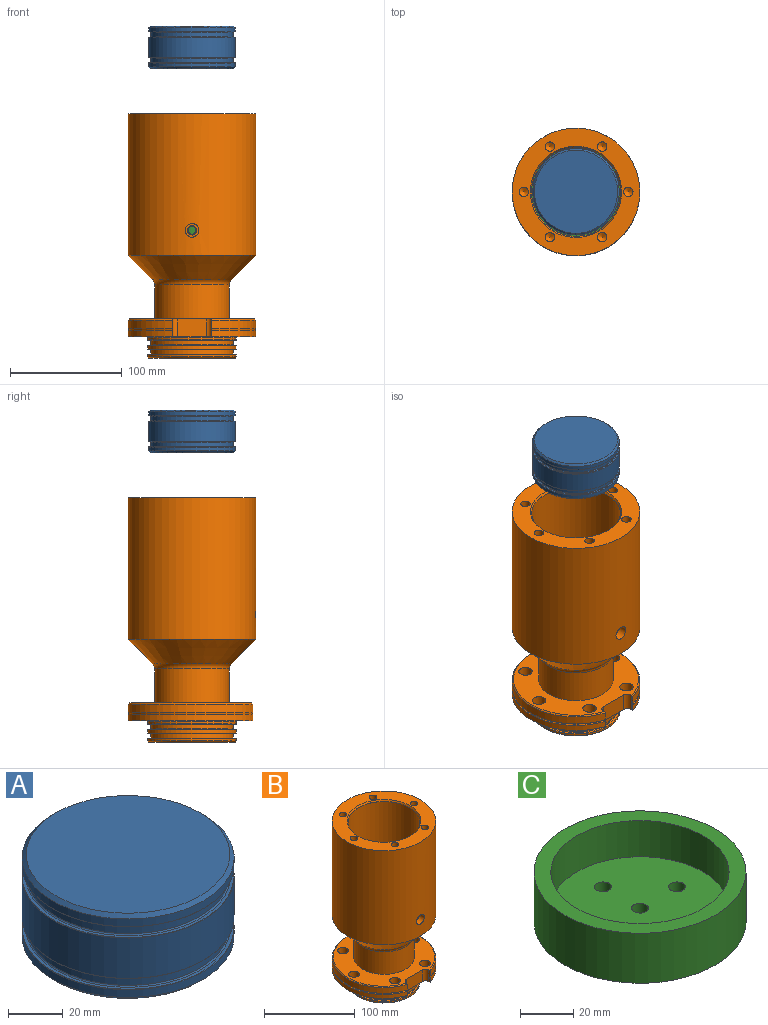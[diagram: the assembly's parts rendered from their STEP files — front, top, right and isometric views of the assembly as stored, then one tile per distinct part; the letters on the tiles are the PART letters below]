
ASSEMBLY  parts=3 mates=2
PART A: 21 faces, bbox 83.9x83.9x38.1 mm
  f0: cylinder r=36.86mm len=73.71mm, axis (0,0,1), area 882.3mm2, adj f1,f20
  f1: torus R=37.36mm, axis (0,0,1), area 185.7mm2, adj f0,f2
  f2: plane 77.22x77.22mm, normal (0,0,1), area 297.1mm2, adj f1,f3
  f3: torus R=38.61mm, axis (0,0,1), area 48.5mm2, adj f2,f4
  f4: cylinder r=38.73mm len=77.47mm, axis (0,0,1), area 4389.1mm2, adj f3,f5
  f5: torus R=38.61mm, axis (0,0,1), area 48.5mm2, adj f4,f6
  f6: plane 77.22x77.22mm, normal (0,0,-1), area 297.1mm2, adj f5,f7
  f7: torus R=37.36mm, axis (0,0,1), area 185.7mm2, adj f6,f8
  f8: cylinder r=36.86mm len=73.71mm, axis (0,0,1), area 882.3mm2, adj f7,f9
  f9: torus R=37.36mm, axis (0,0,1), area 185.7mm2, adj f8,f10
  f10: plane 77.22x77.22mm, normal (0,0,1), area 297.1mm2, adj f9,f11
  f11: torus R=38.61mm, axis (0,0,1), area 48.5mm2, adj f10,f12
  f12: cylinder r=38.73mm len=77.47mm, axis (0,0,1), area 834.5mm2, adj f11,f13
  f13: cone r=38.73mm half-angle=45deg, axis (0,0,1), area 514.2mm2, adj f12,f14
  f14: plane 74.42x74.42mm, normal (0,0,-1), area 4350mm2, adj f13
  f15: plane 74.42x74.42mm, normal (0,0,1), area 4350mm2, adj f16
  f16: cone r=38.73mm half-angle=45deg, axis (0,0,-1), area 514.2mm2, adj f15,f17
  f17: cylinder r=38.73mm len=77.47mm, axis (0,0,1), area 834.5mm2, adj f16,f18
  f18: torus R=38.61mm, axis (0,0,1), area 48.5mm2, adj f17,f19
  f19: plane 77.22x77.22mm, normal (0,0,-1), area 297.1mm2, adj f18,f20
  f20: torus R=37.36mm, axis (0,0,1), area 185.7mm2, adj f0,f19
PART B: 69 faces, bbox 124.9x121.9x218.8 mm
  f0: cylinder r=3.45mm len=7.11mm, axis (0,-1,0), area 153.4mm2, adj f1,f63,f66,f67
  f1: cylinder r=39.74mm len=129.98mm, axis (0,0,-1), area 32416.5mm2, adj f0,f18,f19,f63,f66
  f2: cylinder r=57.15mm len=127mm, axis (0,0,-1), area 45484.2mm2, adj f21,f22,f65
  f3: cylinder r=57.15mm len=114.3mm, axis (0,0,-1), area 2527mm2, adj f6,f7,f58,f59
  f4: cylinder r=57.15mm len=114.3mm, axis (0,0,-1), area 1807.5mm2, adj f7,f8,f58,f59
  f5: plane 112.14x109.34mm, normal (0,0,1), area 5443mm2, adj f6,f24,f52,f53,f54,f55,f56,f57
  f6: cone r=57.15mm half-angle=45deg, axis (0,0,-1), area 487.8mm2, adj f3,f5,f58,f59
  f7: torus R=57.15mm, axis (0,0,-1), area 766.9mm2, adj f3,f4,f58,f59
  f8: plane 114.3x111.55mm, normal (0,0,-1), area 4347.6mm2, adj f4,f25,f52,f53,f54,f55,f56,f57
  f9: plane 79.1x79.1mm, normal (0,0,1), area 521.8mm2, adj f10,f39
  f10: torus R=39.55mm, axis (0,0,-1), area 49.7mm2, adj f9,f11
  f11: cylinder r=39.67mm len=79.35mm, axis (0,0,-1), area 459.5mm2, adj f10,f12
  f12: cone r=39.67mm half-angle=45deg, axis (0,0,1), area 374.7mm2, adj f11,f13
  f13: plane 77.19x77.19mm, normal (0,0,-1), area 1545.2mm2, adj f12,f14
  f14: cone r=31.59mm half-angle=30deg, axis (0,0,-1), area 2572.9mm2, adj f13,f15
  f15: cylinder r=24.26mm len=72.39mm, axis (0,0,-1), area 11033mm2, adj f14,f16
  f16: plane 48.51x48.51mm, normal (0,0,-1), area 57.6mm2, adj f15,f17
  f17: cylinder r=23.88mm len=47.75mm, axis (0,0,-1), area 266.7mm2, adj f16,f18
  f18: plane 79.48x79.48mm, normal (0,0,1), area 3170.1mm2, adj f1,f17
  f19: torus R=39.99mm, axis (0,0,-1), area 33.2mm2, adj f1,f20
  f20: cone r=39.77mm half-angle=30deg, axis (0,0,1), area 539.8mm2, adj f19,f21
  f21: plane 114.3x114.3mm, normal (0,0,1), area 4686.3mm2, adj f2,f20,f41,f43,f45,f47,f49,f51
  f22: cone r=57.15mm half-angle=45deg, axis (0,0,1), area 8987mm2, adj f2,f23
  f23: torus R=39.75mm, axis (0,0,-1), area 1066.5mm2, adj f22,f24
  f24: cylinder r=33.4mm len=66.8mm, axis (0,0,-1), area 6377.7mm2, adj f5,f23
  f25: torus R=39.67mm, axis (0,0,-1), area 394.6mm2, adj f8,f26
  f26: cylinder r=39.67mm len=79.35mm, axis (0,0,-1), area 474.9mm2, adj f25,f27
  f27: torus R=39.55mm, axis (0,0,-1), area 49.7mm2, adj f26,f28
  f28: plane 79.1x79.1mm, normal (0,0,-1), area 521.8mm2, adj f27,f29
  f29: torus R=37.39mm, axis (0,0,-1), area 185.8mm2, adj f28,f30
  f30: cylinder r=36.88mm len=73.76mm, axis (0,0,-1), area 882.9mm2, adj f29,f31
  f31: torus R=37.39mm, axis (0,0,-1), area 185.8mm2, adj f30,f32
  f32: plane 79.1x79.1mm, normal (0,0,1), area 521.8mm2, adj f31,f33
  f33: torus R=39.55mm, axis (0,0,-1), area 49.7mm2, adj f32,f34
  f34: cylinder r=39.67mm len=79.35mm, axis (0,0,-1), area 759.8mm2, adj f33,f35
  f35: torus R=39.55mm, axis (0,0,-1), area 49.7mm2, adj f34,f36
  f36: plane 79.1x79.1mm, normal (0,0,-1), area 521.8mm2, adj f35,f37
  f37: torus R=37.39mm, axis (0,0,-1), area 185.8mm2, adj f36,f38
  f38: cylinder r=36.88mm len=73.76mm, axis (0,0,-1), area 882.9mm2, adj f37,f39
  f39: torus R=37.39mm, axis (0,0,-1), area 185.8mm2, adj f9,f38
  f40: cone r=0mm half-angle=59deg, axis (0,0,1), area 65.2mm2, adj f41
  f41: cylinder r=4.22mm len=34.93mm, axis (0,0,1), area 925.2mm2, adj f21,f40
  f42: cone r=0mm half-angle=59deg, axis (0,0,1), area 65.2mm2, adj f43
  f43: cylinder r=4.22mm len=34.93mm, axis (0,0,1), area 925.2mm2, adj f21,f42
  f44: cone r=0mm half-angle=59deg, axis (0,0,1), area 65.2mm2, adj f45
  f45: cylinder r=4.22mm len=34.93mm, axis (0,0,1), area 925.2mm2, adj f21,f44
  f46: cone r=0mm half-angle=59deg, axis (0,0,1), area 65.2mm2, adj f47
  f47: cylinder r=4.22mm len=34.93mm, axis (0,0,1), area 925.2mm2, adj f21,f46
  f48: cone r=0mm half-angle=59deg, axis (0,0,1), area 65.2mm2, adj f49
  f49: cylinder r=4.22mm len=34.93mm, axis (0,0,1), area 925.2mm2, adj f21,f48
  f50: cone r=0mm half-angle=59deg, axis (0,0,1), area 65.2mm2, adj f51
  f51: cylinder r=4.22mm len=34.93mm, axis (0,0,1), area 925.2mm2, adj f21,f50
  f52: cylinder r=5.97mm len=16mm, axis (0,0,1), area 600.1mm2, adj f5,f8
  f53: cylinder r=5.97mm len=16mm, axis (0,0,1), area 600.1mm2, adj f5,f8
  f54: cylinder r=5.97mm len=16mm, axis (0,0,1), area 600.1mm2, adj f5,f8
  f55: cylinder r=5.97mm len=16mm, axis (0,0,1), area 600.1mm2, adj f5,f8
  f56: cylinder r=5.97mm len=16mm, axis (0,0,1), area 600.1mm2, adj f5,f8
  f57: cylinder r=5.97mm len=16mm, axis (0,0,1), area 600.1mm2, adj f5,f8
  f58: plane 16.01x2.08mm, normal (1,0,0), area 31.6mm2, adj f3,f4,f5,f6,f7,f8,f62
  f59: plane 16.01x2.08mm, normal (-1,0,0), area 31.6mm2, adj f3,f4,f5,f6,f7,f8,f60
  f60: cylinder r=4.83mm len=16mm, axis (0,0,1), area 121.3mm2, adj f5,f8,f59,f61
  f61: plane 25.4x16mm, normal (0,-1,0), area 406.5mm2, adj f5,f8,f60,f62
  f62: cylinder r=4.83mm len=16mm, axis (0,0,1), area 121.3mm2, adj f5,f8,f58,f61
  f63: cone r=0mm half-angle=59deg, axis (0,-1,0), area 0.1mm2, adj f0,f1
  f64: plane 12.29x12.29mm, normal (0,-1,0), area 64.2mm2, adj f65,f68
  f65: cylinder r=6.15mm len=12.29mm, axis (0,-1,0), area 307.5mm2, adj f2,f64
  f66: cone r=0mm half-angle=59deg, axis (0,-1,0), area 0.1mm2, adj f0,f1
  f67: plane 8.33x8.33mm, normal (0,-1,0), area 17mm2, adj f0,f68
  f68: cylinder r=4.17mm len=8.33mm, axis (0,-1,0), area 59.8mm2, adj f64,f67
PART C: 10 faces, bbox 79.7x79.7x23 mm
  f0: plane 79.73x79.73mm, normal (0,0,-1), area 4834.4mm2, adj f4,f5,f6,f7,f8,f9
  f1: plane 67.03x67.03mm, normal (0,0,1), area 3370.5mm2, adj f2,f5,f6,f7,f8,f9
  f2: cylinder r=33.52mm len=67.03mm, axis (0,0,-1), area 3503.5mm2, adj f1,f3
  f3: plane 79.73x79.73mm, normal (0,0,1), area 1463.9mm2, adj f2,f4
  f4: cylinder r=39.87mm len=79.73mm, axis (0,0,-1), area 5757.8mm2, adj f0,f3
  f5: cylinder r=3.17mm len=6.35mm, axis (0,0,1), area 126.7mm2, adj f0,f1
  f6: cylinder r=3.17mm len=6.35mm, axis (0,0,1), area 126.7mm2, adj f0,f1
  f7: cylinder r=3.17mm len=6.35mm, axis (0,0,1), area 126.7mm2, adj f0,f1
  f8: cylinder r=3.17mm len=6.35mm, axis (0,0,1), area 126.7mm2, adj f0,f1
  f9: cylinder r=3.17mm len=6.35mm, axis (0,0,1), area 126.7mm2, adj f0,f1
PLACE A rot(axis=(0,0,-1),90deg) t=(39.67,0,259.2)mm
PLACE B at identity fixed
PLACE C rot(axis=(0,1,0),180deg) t=(39.67,0,125.34)mm
MATE slider C.f2 <-> B.f6  axis (0,0,1) through (39.67,0,113.85)mm
MATE slider A.f0 <-> B.f6  axis (0,0,1) through (39.67,0,278.25)mm
